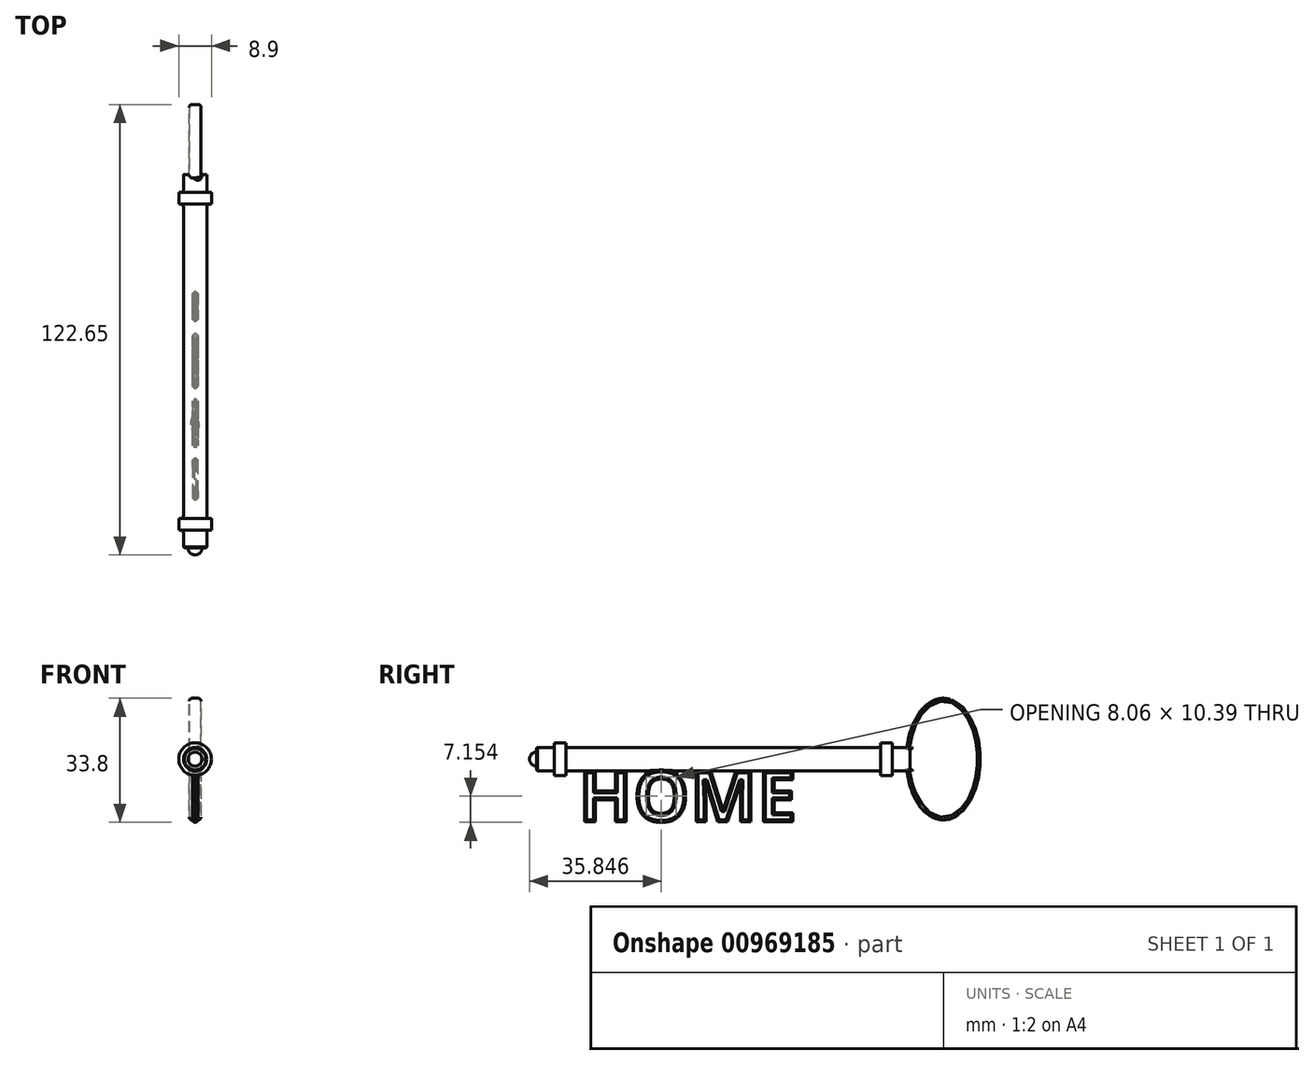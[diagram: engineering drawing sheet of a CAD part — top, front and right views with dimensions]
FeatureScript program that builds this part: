
annotation { "Feature Type Name" : "Feature", "Feature Type Description" : "" }
export const myFeature = defineFeature(function(context is Context, id is Id, definition is map)
    precondition{}
    {
        {
            var Q0;
            Q0=qCreatedBy(makeId("Right.planeOp"),FACE);
            var sketch = newSketch(context, id + "F0", { "sketchPlane" : qUnion([Q0])});
            skLineSegment(sketch, "E0", {"start": v(161.73, 0) * mm, "end": v(-150.5, 0) * mm, "construction": true});
            skLineSegment(sketch, "E1.bottom", {"start": v(0, 0) * mm, "end": v(-101.6, 0) * mm});
            skLineSegment(sketch, "E1.top", {"start": v(0, 3.17) * mm, "end": v(-4.86, 3.17) * mm});
            skLineSegment(sketch, "E1.left", {"start": v(0, 0) * mm, "end": v(0, 3.17) * mm});
            skLineSegment(sketch, "E1.right", {"start": v(-101.6, 1.9) * mm, "end": v(-101.6, 3.17) * mm});
            skLineSegment(sketch, "E2.bottom", {"start": v(-96.74, 4.45) * mm, "end": v(-93.57, 4.44) * mm});
            skLineSegment(sketch, "E2.left", {"start": v(-96.74, 4.44) * mm, "end": v(-96.74, 3.17) * mm});
            skLineSegment(sketch, "E2.right", {"start": v(-93.57, 4.44) * mm, "end": v(-93.57, 3.17) * mm});
            skPoint(sketch, "E2.middle", {"position": v(-95.15, 3.17) * mm});
            skLineSegment(sketch, "E3", {"start": v(-50.8, 3.17) * mm, "end": v(-50.8, 19.65) * mm, "construction": true});
            skLineSegment(sketch, "E4.MirrorCS", {"start": v(-8.03, 4.44) * mm, "end": v(-8.03, 3.17) * mm});
            skLineSegment(sketch, "E5.MirrorCS", {"start": v(-4.86, 4.44) * mm, "end": v(-4.86, 3.17) * mm});
            skLineSegment(sketch, "E6.MirrorCS", {"start": v(-4.86, 4.45) * mm, "end": v(-8.03, 4.44) * mm});
            skPoint(sketch, "E7.MirrorP", {"position": v(-6.45, 3.17) * mm});
            skArc(sketch, "E8", {"start": v(-101.6, 1.9) * mm, "mid": v(-102.95, 1.35) * mm, "end": v(-103.5, 0) * mm});
            skLineSegment(sketch, "E9", {"start": v(-103.5, 0) * mm, "end": v(-101.6, 0) * mm});
            skPoint(sketch, "E10.orphan", {"position": v(-96.74, 1.9) * mm});
            skLineSegment(sketch, "E11.trimOffspring", {"start": v(-96.74, 3.17) * mm, "end": v(-101.6, 3.17) * mm});
            skPoint(sketch, "E12.orphan", {"position": v(-93.57, 1.9) * mm});
            skPoint(sketch, "E13.orphan", {"position": v(-8.03, 1.9) * mm});
            skLineSegment(sketch, "E14.trimOffspring", {"start": v(-8.03, 3.17) * mm, "end": v(-93.57, 3.17) * mm});
            skPoint(sketch, "E15.orphan", {"position": v(-4.86, 1.9) * mm});
            skSolve(sketch);
        }
        {
            var Q0;
            Q0=makeQuery(id+"F0.imprint","IMPRINT",FACE,{"disambiguationData":[TD([[makeQuery(id+"F0.imprint","IMPRINT",EDGE,{"derivedFrom":sQuery(id+"F0.wireOp",EDGE,"E1.bottom")}),-1.0]])]});
            var Q1;
            Q1=sQuery(id+"F0.wireOp",EDGE,"E0");
            revolve(context, id + "F1", {"surfaceOperationType" : NewSurfaceOperationType.NEW, "entities" : qUnion([Q0]), "axis" : qUnion([Q1]), "revolveType" : RevolveType.FULL});
        }
        {
            var Q0;
            Q0=qCreatedBy(makeId("Right.planeOp"),FACE);
            var sketch = newSketch(context, id + "F2", { "sketchPlane" : qUnion([Q0])});
            skEllipse(sketch, "E16", {"center": v(9.06, 0) * mm, "majorRadius": 16.57 * mm, "minorRadius": 10.08 * mm, "majorAxis": v(0, 1)});
            skFitSpline(sketch, "E17.0", {"points": [v(10.06, 13.42) * mm, v(9.06, 13.57) * mm, v(8.06, 13.42) * mm, v(7.12, 12.97) * mm, v(6.32, 12.35) * mm, v(5.5, 11.55) * mm, v(4.51, 10.21) * mm, v(3.64, 8.48) * mm, v(3.06, 6.88) * mm, v(2.57, 5.18) * mm, v(2.23, 3.35) * mm, v(2.06, 1.45) * mm, v(2.01, 0) * mm, v(2.06, -1.45) * mm, v(2.23, -3.35) * mm, v(2.57, -5.18) * mm, v(3.06, -6.88) * mm, v(3.64, -8.48) * mm, v(4.51, -10.21) * mm, v(5.5, -11.55) * mm, v(6.32, -12.35) * mm, v(7.12, -12.97) * mm, v(8.06, -13.42) * mm, v(9.06, -13.57) * mm, v(10.06, -13.42) * mm, v(11, -12.97) * mm, v(11.8, -12.35) * mm, v(12.6, -11.55) * mm, v(13.6, -10.21) * mm, v(14.48, -8.48) * mm, v(15.06, -6.88) * mm, v(15.55, -5.18) * mm, v(15.89, -3.35) * mm, v(16.06, -1.45) * mm, v(16.1, 0) * mm, v(16.06, 1.45) * mm, v(15.89, 3.35) * mm, v(15.55, 5.18) * mm, v(15.06, 6.88) * mm, v(14.48, 8.48) * mm, v(13.6, 10.21) * mm, v(12.6, 11.55) * mm, v(11.8, 12.35) * mm, v(11, 12.97) * mm, v(10.06, 13.42) * mm, v(9.06, 13.57) * mm, v(8.06, 13.42) * mm, v(10.06, 13.42) * mm]});
            skSolve(sketch);
        }
        {
            var Q0;
            Q0 = qSketchRegion(id + "F2", true);
            extrude(context, id + "F3", {"entities" : qUnion([Q0]), "operationType" : NewBodyOperationType.ADD, "endBound" : BoundingType.SYMMETRIC, "depth" : 3.17 * mm, "offsetDistance" : 25.4 * mm});
        }
        {
            var Q0;
            Q0=makeQuery(id+"F3.opExtrude","CAP_FACE",FACE,{"disambiguationData":[OSD([sQuery(id+"F2.wireOp",EDGE,"E16"),sQuery(id+"F2.wireOp",EDGE,"E17.0")])],"isStart":false});
            var Q1;
            Q1=makeQuery(id+"F3.opExtrude","CAP_EDGE",EDGE,{"disambiguationData":[OSD([sQuery(id+"F2.wireOp",EDGE,"E17.0")])],"isStart":true});
            var Q2;
            Q2=makeQuery(id+"F3.opExtrude","CAP_EDGE",EDGE,{"disambiguationData":[OSD([sQuery(id+"F2.wireOp",EDGE,"E16")])],"isStart":true});
            fillet(context, id + "F4", {"entities" : qUnion([Q0, Q1, Q2]), "radius" : 0.76 * mm, "tangentPropagation" : true, "allowEdgeOverflow" : false});
        }
        {
            var Q0;
            Q0=makeQuery(id+"F1.opRevolve","SWEPT_EDGE",EDGE,{"disambiguationData":[OSD([sQuery(id+"F0.wireOp",EDGE,"E4.MirrorCS"),sQuery(id+"F0.wireOp",EDGE,"E14.trimOffspring")])]});
            var Q1;
            Q1=makeQuery(id+"F1.opRevolve","SWEPT_EDGE",EDGE,{"disambiguationData":[OSD([sQuery(id+"F0.wireOp",EDGE,"E1.top"),sQuery(id+"F0.wireOp",EDGE,"E5.MirrorCS")])]});
            var Q2;
            Q2=makeQuery(id+"F1.opRevolve","SWEPT_EDGE",EDGE,{"disambiguationData":[OSD([sQuery(id+"F0.wireOp",EDGE,"E2.right"),sQuery(id+"F0.wireOp",EDGE,"E14.trimOffspring")])]});
            var Q3;
            Q3=makeQuery(id+"F1.opRevolve","SWEPT_EDGE",EDGE,{"disambiguationData":[OSD([sQuery(id+"F0.wireOp",EDGE,"E2.left"),sQuery(id+"F0.wireOp",EDGE,"E11.trimOffspring")])]});
            fillet(context, id + "F5", {"entities" : qUnion([Q0, Q1, Q2, Q3]), "radius" : 0.76 * mm, "tangentPropagation" : true, "allowEdgeOverflow" : false});
        }
        {
            var Q0;
            Q0=makeQuery(id+"F1.opRevolve","SWEPT_EDGE",EDGE,{"disambiguationData":[OSD([sQuery(id+"F0.wireOp",EDGE,"E1.right"),sQuery(id+"F0.wireOp",EDGE,"E11.trimOffspring")])]});
            chamfer(context, id + "F6", {"entities" : qUnion([Q0]), "width" : 0.25 * mm, "tangentPropagation" : true});
        }
        {
            var Q0;
            Q0=qCreatedBy(makeId("Right.planeOp"),FACE);
            var sketch = newSketch(context, id + "F7", { "sketchPlane" : qUnion([Q0])});
            skText(sketch, "E18", { "text": "HOME", "fontName": "OpenSans-Bold.ttf"});
            const initialGuessF7  = {"E18": [-0.09028, -0.01704, 1, 0, 0.014]};
            skSetInitialGuess(sketch, initialGuessF7);
            skSolve(sketch);
        }
        {
            var Q0;
            Q0 = qSketchRegion(id + "F7", true);
            extrude(context, id + "F8", {"entities" : qUnion([Q0]), "operationType" : NewBodyOperationType.ADD, "endBound" : BoundingType.SYMMETRIC, "depth" : 1.52 * mm, "offsetDistance" : 25.4 * mm});
        }
        {
            var Q0;
            Q0=makeQuery(id+"F8.opExtrude","CAP_FACE",FACE,{"disambiguationData":[OSD([sQuery(id+"F7.wireOp",EDGE,"E18.sketch_text.stroke-45"),sQuery(id+"F7.wireOp",EDGE,"E18.sketch_text.stroke-46"),sQuery(id+"F7.wireOp",EDGE,"E18.sketch_text.stroke-47"),sQuery(id+"F7.wireOp",EDGE,"E18.sketch_text.stroke-48"),sQuery(id+"F7.wireOp",EDGE,"E18.sketch_text.stroke-49"),sQuery(id+"F7.wireOp",EDGE,"E18.sketch_text.stroke-50"),sQuery(id+"F7.wireOp",EDGE,"E18.sketch_text.stroke-51"),sQuery(id+"F7.wireOp",EDGE,"E18.sketch_text.stroke-52"),sQuery(id+"F7.wireOp",EDGE,"E18.sketch_text.stroke-53"),sQuery(id+"F7.wireOp",EDGE,"E18.sketch_text.stroke-54"),sQuery(id+"F7.wireOp",EDGE,"E18.sketch_text.stroke-55"),sQuery(id+"F7.wireOp",EDGE,"E18.sketch_text.stroke-56")])],"isStart":false});
            var Q1;
            Q1=makeQuery(id+"F8.opExtrude","CAP_FACE",FACE,{"disambiguationData":[OSD([sQuery(id+"F7.wireOp",EDGE,"E18.sketch_text.stroke-0"),sQuery(id+"F7.wireOp",EDGE,"E18.sketch_text.stroke-1"),sQuery(id+"F7.wireOp",EDGE,"E18.sketch_text.stroke-2"),sQuery(id+"F7.wireOp",EDGE,"E18.sketch_text.stroke-3"),sQuery(id+"F7.wireOp",EDGE,"E18.sketch_text.stroke-4"),sQuery(id+"F7.wireOp",EDGE,"E18.sketch_text.stroke-5"),sQuery(id+"F7.wireOp",EDGE,"E18.sketch_text.stroke-6"),sQuery(id+"F7.wireOp",EDGE,"E18.sketch_text.stroke-7"),sQuery(id+"F7.wireOp",EDGE,"E18.sketch_text.stroke-8"),sQuery(id+"F7.wireOp",EDGE,"E18.sketch_text.stroke-9"),sQuery(id+"F7.wireOp",EDGE,"E18.sketch_text.stroke-10"),sQuery(id+"F7.wireOp",EDGE,"E18.sketch_text.stroke-11")])],"isStart":false});
            var Q2;
            Q2=makeQuery(id+"F8.opExtrude","CAP_FACE",FACE,{"disambiguationData":[OSD([sQuery(id+"F7.wireOp",EDGE,"E18.sketch_text.stroke-12"),sQuery(id+"F7.wireOp",EDGE,"E18.sketch_text.stroke-13"),sQuery(id+"F7.wireOp",EDGE,"E18.sketch_text.stroke-14"),sQuery(id+"F7.wireOp",EDGE,"E18.sketch_text.stroke-15"),sQuery(id+"F7.wireOp",EDGE,"E18.sketch_text.stroke-16"),sQuery(id+"F7.wireOp",EDGE,"E18.sketch_text.stroke-17"),sQuery(id+"F7.wireOp",EDGE,"E18.sketch_text.stroke-18"),sQuery(id+"F7.wireOp",EDGE,"E18.sketch_text.stroke-19"),sQuery(id+"F7.wireOp",EDGE,"E18.sketch_text.stroke-20"),sQuery(id+"F7.wireOp",EDGE,"E18.sketch_text.stroke-21"),sQuery(id+"F7.wireOp",EDGE,"E18.sketch_text.stroke-22"),sQuery(id+"F7.wireOp",EDGE,"E18.sketch_text.stroke-23"),sQuery(id+"F7.wireOp",EDGE,"E18.sketch_text.stroke-24"),sQuery(id+"F7.wireOp",EDGE,"E18.sketch_text.stroke-25")])],"isStart":false});
            var Q3;
            Q3=makeQuery(id+"F8.opExtrude","CAP_FACE",FACE,{"disambiguationData":[OSD([sQuery(id+"F7.wireOp",EDGE,"E18.sketch_text.stroke-26"),sQuery(id+"F7.wireOp",EDGE,"E18.sketch_text.stroke-27"),sQuery(id+"F7.wireOp",EDGE,"E18.sketch_text.stroke-28"),sQuery(id+"F7.wireOp",EDGE,"E18.sketch_text.stroke-29"),sQuery(id+"F7.wireOp",EDGE,"E18.sketch_text.stroke-30"),sQuery(id+"F7.wireOp",EDGE,"E18.sketch_text.stroke-31"),sQuery(id+"F7.wireOp",EDGE,"E18.sketch_text.stroke-32"),sQuery(id+"F7.wireOp",EDGE,"E18.sketch_text.stroke-33"),sQuery(id+"F7.wireOp",EDGE,"E18.sketch_text.stroke-34"),sQuery(id+"F7.wireOp",EDGE,"E18.sketch_text.stroke-35"),sQuery(id+"F7.wireOp",EDGE,"E18.sketch_text.stroke-36"),sQuery(id+"F7.wireOp",EDGE,"E18.sketch_text.stroke-37"),sQuery(id+"F7.wireOp",EDGE,"E18.sketch_text.stroke-38"),sQuery(id+"F7.wireOp",EDGE,"E18.sketch_text.stroke-39"),sQuery(id+"F7.wireOp",EDGE,"E18.sketch_text.stroke-40"),sQuery(id+"F7.wireOp",EDGE,"E18.sketch_text.stroke-41"),sQuery(id+"F7.wireOp",EDGE,"E18.sketch_text.stroke-42"),sQuery(id+"F7.wireOp",EDGE,"E18.sketch_text.stroke-43"),sQuery(id+"F7.wireOp",EDGE,"E18.sketch_text.stroke-44")])],"isStart":false});
            var Q4;
            Q4=makeQuery(id+"F8.opExtrude","CAP_FACE",FACE,{"disambiguationData":[OSD([sQuery(id+"F7.wireOp",EDGE,"E18.sketch_text.stroke-0"),sQuery(id+"F7.wireOp",EDGE,"E18.sketch_text.stroke-1"),sQuery(id+"F7.wireOp",EDGE,"E18.sketch_text.stroke-2"),sQuery(id+"F7.wireOp",EDGE,"E18.sketch_text.stroke-3"),sQuery(id+"F7.wireOp",EDGE,"E18.sketch_text.stroke-4"),sQuery(id+"F7.wireOp",EDGE,"E18.sketch_text.stroke-5"),sQuery(id+"F7.wireOp",EDGE,"E18.sketch_text.stroke-6"),sQuery(id+"F7.wireOp",EDGE,"E18.sketch_text.stroke-7"),sQuery(id+"F7.wireOp",EDGE,"E18.sketch_text.stroke-8"),sQuery(id+"F7.wireOp",EDGE,"E18.sketch_text.stroke-9"),sQuery(id+"F7.wireOp",EDGE,"E18.sketch_text.stroke-10"),sQuery(id+"F7.wireOp",EDGE,"E18.sketch_text.stroke-11")])],"isStart":true});
            var Q5;
            Q5=makeQuery(id+"F8.opExtrude","CAP_FACE",FACE,{"disambiguationData":[OSD([sQuery(id+"F7.wireOp",EDGE,"E18.sketch_text.stroke-12"),sQuery(id+"F7.wireOp",EDGE,"E18.sketch_text.stroke-13"),sQuery(id+"F7.wireOp",EDGE,"E18.sketch_text.stroke-14"),sQuery(id+"F7.wireOp",EDGE,"E18.sketch_text.stroke-15"),sQuery(id+"F7.wireOp",EDGE,"E18.sketch_text.stroke-16"),sQuery(id+"F7.wireOp",EDGE,"E18.sketch_text.stroke-17"),sQuery(id+"F7.wireOp",EDGE,"E18.sketch_text.stroke-18"),sQuery(id+"F7.wireOp",EDGE,"E18.sketch_text.stroke-19"),sQuery(id+"F7.wireOp",EDGE,"E18.sketch_text.stroke-20"),sQuery(id+"F7.wireOp",EDGE,"E18.sketch_text.stroke-21"),sQuery(id+"F7.wireOp",EDGE,"E18.sketch_text.stroke-22"),sQuery(id+"F7.wireOp",EDGE,"E18.sketch_text.stroke-23"),sQuery(id+"F7.wireOp",EDGE,"E18.sketch_text.stroke-24"),sQuery(id+"F7.wireOp",EDGE,"E18.sketch_text.stroke-25")])],"isStart":true});
            var Q6;
            Q6=makeQuery(id+"F8.opExtrude","CAP_FACE",FACE,{"disambiguationData":[OSD([sQuery(id+"F7.wireOp",EDGE,"E18.sketch_text.stroke-26"),sQuery(id+"F7.wireOp",EDGE,"E18.sketch_text.stroke-27"),sQuery(id+"F7.wireOp",EDGE,"E18.sketch_text.stroke-28"),sQuery(id+"F7.wireOp",EDGE,"E18.sketch_text.stroke-29"),sQuery(id+"F7.wireOp",EDGE,"E18.sketch_text.stroke-30"),sQuery(id+"F7.wireOp",EDGE,"E18.sketch_text.stroke-31"),sQuery(id+"F7.wireOp",EDGE,"E18.sketch_text.stroke-32"),sQuery(id+"F7.wireOp",EDGE,"E18.sketch_text.stroke-33"),sQuery(id+"F7.wireOp",EDGE,"E18.sketch_text.stroke-34"),sQuery(id+"F7.wireOp",EDGE,"E18.sketch_text.stroke-35"),sQuery(id+"F7.wireOp",EDGE,"E18.sketch_text.stroke-36"),sQuery(id+"F7.wireOp",EDGE,"E18.sketch_text.stroke-37"),sQuery(id+"F7.wireOp",EDGE,"E18.sketch_text.stroke-38"),sQuery(id+"F7.wireOp",EDGE,"E18.sketch_text.stroke-39"),sQuery(id+"F7.wireOp",EDGE,"E18.sketch_text.stroke-40"),sQuery(id+"F7.wireOp",EDGE,"E18.sketch_text.stroke-41"),sQuery(id+"F7.wireOp",EDGE,"E18.sketch_text.stroke-42"),sQuery(id+"F7.wireOp",EDGE,"E18.sketch_text.stroke-43"),sQuery(id+"F7.wireOp",EDGE,"E18.sketch_text.stroke-44")])],"isStart":true});
            var Q7;
            Q7=makeQuery(id+"F8.opExtrude","CAP_FACE",FACE,{"disambiguationData":[OSD([sQuery(id+"F7.wireOp",EDGE,"E18.sketch_text.stroke-45"),sQuery(id+"F7.wireOp",EDGE,"E18.sketch_text.stroke-46"),sQuery(id+"F7.wireOp",EDGE,"E18.sketch_text.stroke-47"),sQuery(id+"F7.wireOp",EDGE,"E18.sketch_text.stroke-48"),sQuery(id+"F7.wireOp",EDGE,"E18.sketch_text.stroke-49"),sQuery(id+"F7.wireOp",EDGE,"E18.sketch_text.stroke-50"),sQuery(id+"F7.wireOp",EDGE,"E18.sketch_text.stroke-51"),sQuery(id+"F7.wireOp",EDGE,"E18.sketch_text.stroke-52"),sQuery(id+"F7.wireOp",EDGE,"E18.sketch_text.stroke-53"),sQuery(id+"F7.wireOp",EDGE,"E18.sketch_text.stroke-54"),sQuery(id+"F7.wireOp",EDGE,"E18.sketch_text.stroke-55"),sQuery(id+"F7.wireOp",EDGE,"E18.sketch_text.stroke-56")])],"isStart":true});
            chamfer(context, id + "F9", {"entities" : qUnion([Q0, Q1, Q2, Q3, Q4, Q5, Q6, Q7]), "width" : 0.5 * mm, "tangentPropagation" : true});
        }
    });
